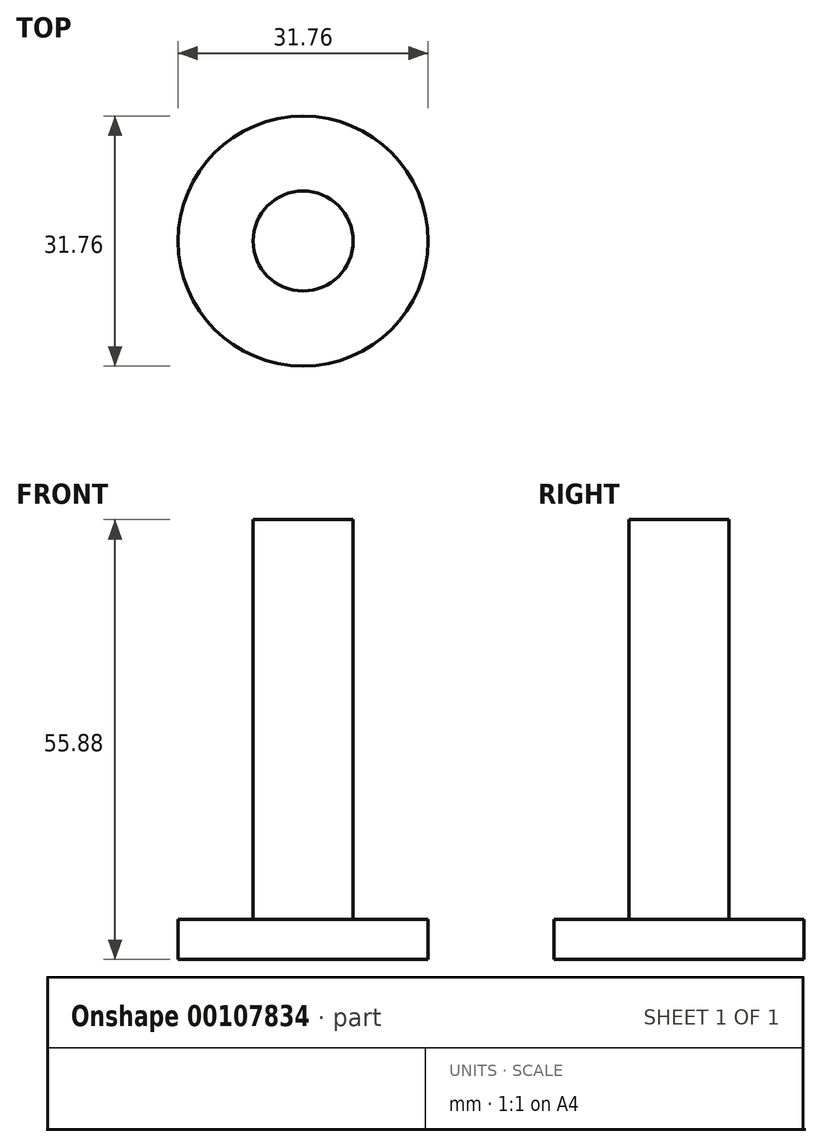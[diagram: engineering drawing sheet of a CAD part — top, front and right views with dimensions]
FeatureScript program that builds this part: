
annotation { "Feature Type Name" : "Feature", "Feature Type Description" : "" }
export const myFeature = defineFeature(function(context is Context, id is Id, definition is map)
    precondition{}
    {
        {
            var Q0;
            Q0=qCreatedBy(makeId("Front.planeOp"),FACE);
            var sketch = newSketch(context, id + "F0", { "sketchPlane" : qUnion([Q0])});
            skLineSegment(sketch, "E0.bottom", {"start": v(0, 0) * mm, "end": v(6.35, 0) * mm});
            skLineSegment(sketch, "E0.top", {"start": v(0, 50.8) * mm, "end": v(6.35, 50.8) * mm});
            skLineSegment(sketch, "E0.left", {"start": v(0, 0) * mm, "end": v(0, 50.8) * mm});
            skLineSegment(sketch, "E0.right", {"start": v(6.35, 0) * mm, "end": v(6.35, 50.8) * mm});
            skSolve(sketch);
        }
        {
            var Q0;
            Q0=makeQuery(id+"F0.imprint","IMPRINT",FACE,{"disambiguationData":[TD([[makeQuery(id+"F0.imprint","IMPRINT",EDGE,{"derivedFrom":sQuery(id+"F0.wireOp",EDGE,"E0.bottom")}),1.0]])]});
            var Q1;
            Q1=sQuery(id+"F0.wireOp",EDGE,"E0.left");
            revolve(context, id + "F1", {"entities" : qUnion([Q0]), "axis" : qUnion([Q1]), "revolveType" : RevolveType.FULL});
        }
        {
            var Q0;
            Q0=qCreatedBy(makeId("Top.planeOp"),FACE);
            var sketch = newSketch(context, id + "F2", { "sketchPlane" : qUnion([Q0])});
            skCircle(sketch, "E1", {"center": v(0, 0) * mm, "radius": 15.88 * mm});
            skSolve(sketch);
        }
        {
            var Q0;
            Q0 = qSketchRegion(id + "F2", true);
            extrude(context, id + "F3", {"entities" : qUnion([Q0]), "operationType" : NewBodyOperationType.ADD, "oppositeDirection" : true, "depth" : 5.08 * mm});
        }
    });
